# Revit family: Accessory_Casing_Dunbarton_Casing-Window
name_source: partatom
category: Generic Models
units: mm (PartAtom-declared; Revit-internal decimal feet)

## family parameters
Always vertical = No
Can host rebar = No
Classification Number = 23.30.10.17.17
Cut with Voids When Loaded = No
Maintain Annotation Orientation = No
Part Type = Normal
Room Calculation Point = No
Round Connector Dimension = Use Diameter
Shared = No
Work Plane-Based = Yes

## types (3) — shared parameters
Assembly Code = C1020100
Default Elevation = 0' - 0"
Green Building-LEED = http://www.arcat.com
Installation-Fabrication = https://dunbarton.com
Keynote = 08 11 10
Manufacturer = Dunbarton Corporation
Manufacturer Fax = 334-793-7022
Manufacturer Website = https://dunbarton.com
Product Data = http://www.arcat.com
Product Properties = https://dunbarton.com
Revision = R1_08-2016
Sales Information = https://dunbarton.com
Specification = http://www.arcat.com
URL = https://dunbarton.com
zero-valued in all types: Expected Lifespan (Years), Maintenance Schedule (Months), Warranty Duration (Years)

## per-type parameters (varying)
| type | Aluminum | Description | Steel |
| Aluminum | Yes | Dunbarton Casing - Aluminum as Specified | No |
| Steel | No | Dunbarton Casing - Steel as Specified | Yes |
| Steel Colonial | No | Dunbarton Casing - Steel Colonial as Specified | No |

note: column(s) folded — value = type name in every type: Model

type visibility flags (boolean, named after types; folded from table):
- Aluminum: Yes: (none)
- Steel: Yes: (none)
- Steel Colonial: Yes: Steel Colonial

## geometry (parser evidence)
native form markers: Sweep x2
no freeform markers — native parametric forms only
